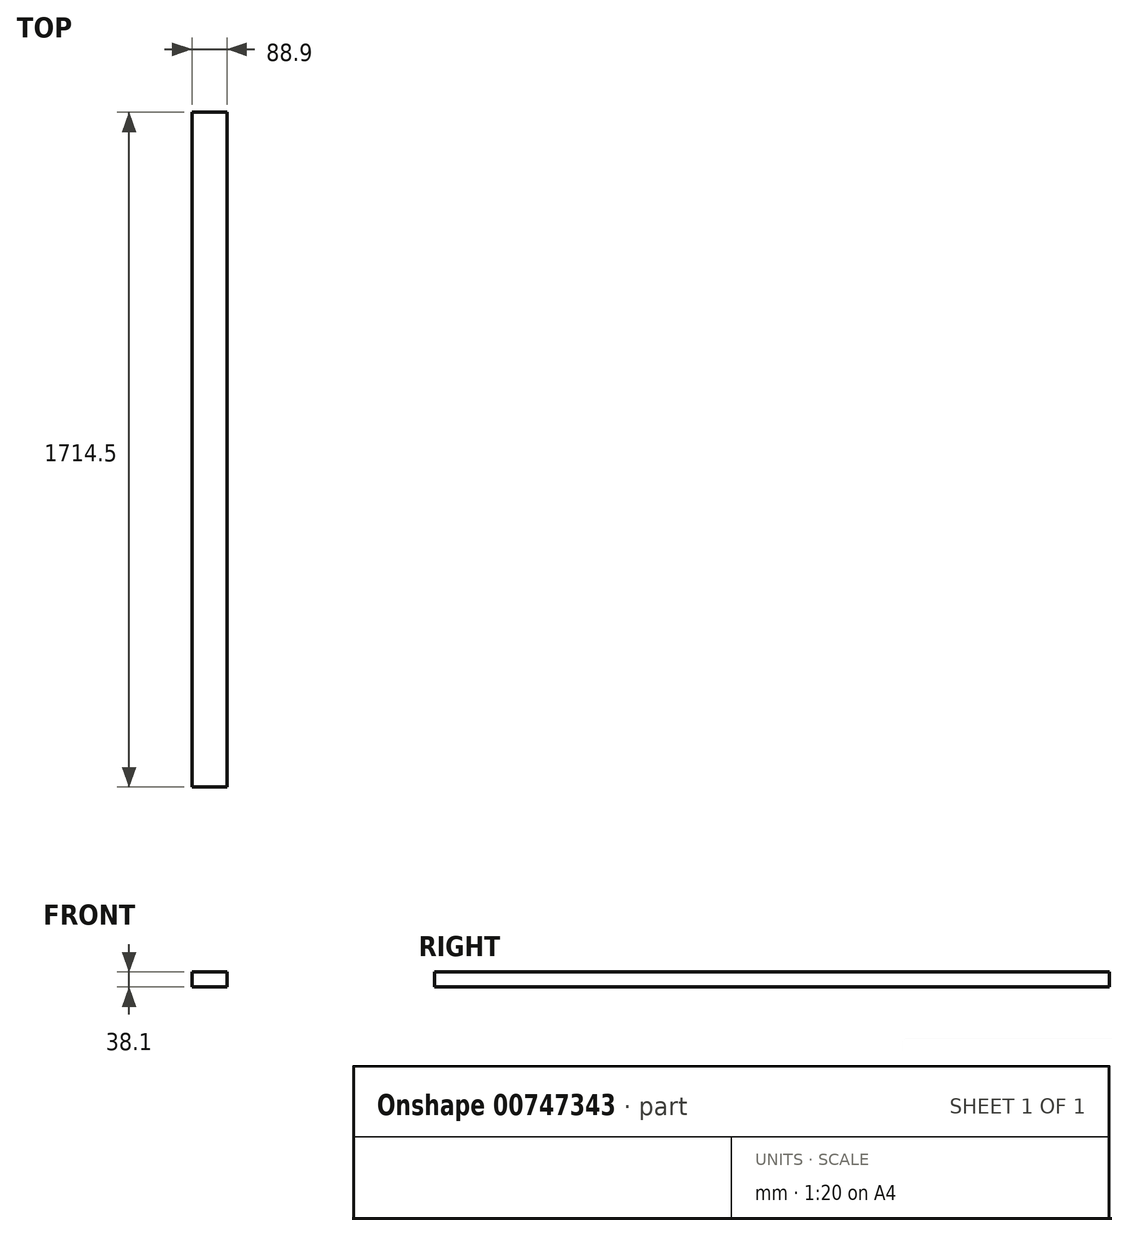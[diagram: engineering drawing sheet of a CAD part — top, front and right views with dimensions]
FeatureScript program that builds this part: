
annotation { "Feature Type Name" : "Feature", "Feature Type Description" : "" }
export const myFeature = defineFeature(function(context is Context, id is Id, definition is map)
    precondition{}
    {
        {
            var Q0;
            Q0=qCreatedBy(makeId("Front.planeOp"),FACE);
            var sketch = newSketch(context, id + "F0", { "sketchPlane" : qUnion([Q0])});
            skLineSegment(sketch, "E0.bottom", {"start": v(0, 0) * mm, "end": v(88.9, 0) * mm});
            skLineSegment(sketch, "E0.top", {"start": v(0, 38.1) * mm, "end": v(88.9, 38.1) * mm});
            skLineSegment(sketch, "E0.left", {"start": v(0, 0) * mm, "end": v(0, 38.1) * mm});
            skLineSegment(sketch, "E0.right", {"start": v(88.9, 0) * mm, "end": v(88.9, 38.1) * mm});
            skSolve(sketch);
        }
        {
            var Q0;
            Q0=qSketchRegion(id+"F0",true);
            extrude(context, id + "F1", {"entities" : qUnion([Q0]), "depth" : 1714.5 * mm, "offsetDistance" : 25.4 * mm});
        }
    });
